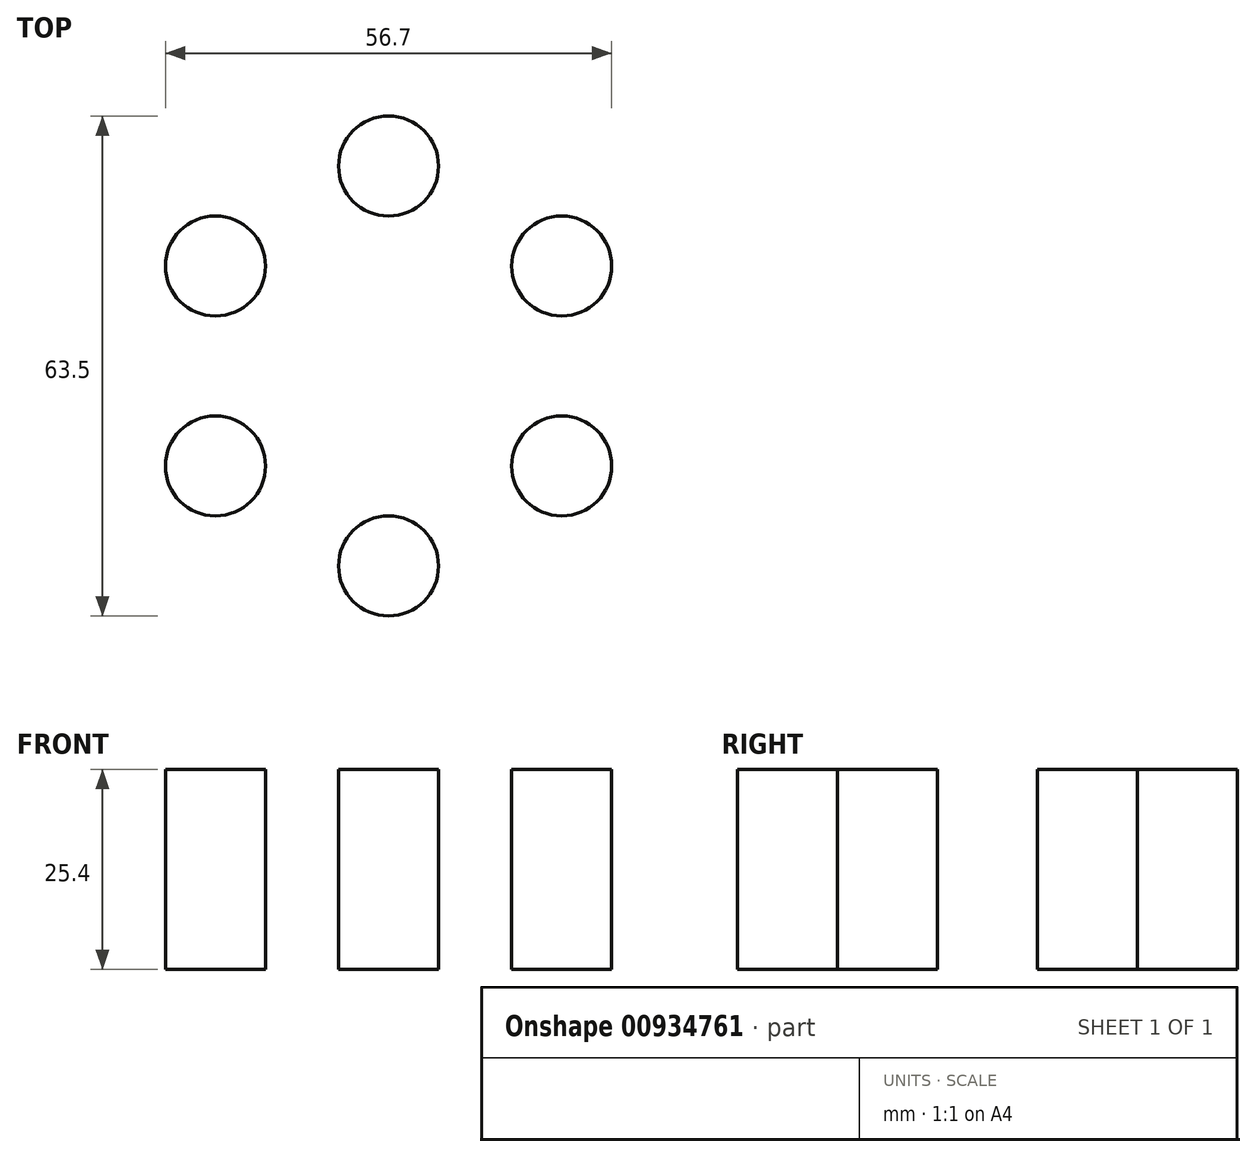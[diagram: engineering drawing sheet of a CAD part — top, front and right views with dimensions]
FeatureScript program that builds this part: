
annotation { "Feature Type Name" : "Feature", "Feature Type Description" : "" }
export const myFeature = defineFeature(function(context is Context, id is Id, definition is map)
    precondition{}
    {
        {
            var Q0;
            Q0=qCreatedBy(makeId("Top.planeOp"),FACE);
            var sketch = newSketch(context, id + "F0", { "sketchPlane" : qUnion([Q0])});
            skCircle(sketch, "E0.cCircle", {"center": v(0, 0) * mm, "radius": 22 * mm, "construction": true});
            skLineSegment(sketch, "E0.0", {"start": v(22, 12.7) * mm, "end": v(22, -12.7) * mm, "construction": true});
            skLineSegment(sketch, "E0.1", {"start": v(22, -12.7) * mm, "end": v(0, -25.4) * mm, "construction": true});
            skLineSegment(sketch, "E0.2", {"start": v(0, -25.4) * mm, "end": v(-22, -12.7) * mm, "construction": true});
            skLineSegment(sketch, "E0.3", {"start": v(-22, -12.7) * mm, "end": v(-22, 12.7) * mm, "construction": true});
            skLineSegment(sketch, "E0.4", {"start": v(-22, 12.7) * mm, "end": v(0, 25.4) * mm, "construction": true});
            skLineSegment(sketch, "E0.5", {"start": v(0, 25.4) * mm, "end": v(22, 12.7) * mm, "construction": true});
            skPoint(sketch, "E0.0.midPoint", {"position": v(22, 0) * mm});
            skCircle(sketch, "E1", {"center": v(0, 25.4) * mm, "radius": 6.35 * mm});
            skCircle(sketch, "E2.1.0", {"center": v(-22, -12.7) * mm, "radius": 6.35 * mm});
            skCircle(sketch, "E2.2.0", {"center": v(22, -12.7) * mm, "radius": 6.35 * mm});
            skCircle(sketch, "E3.1.0", {"center": v(22, 12.7) * mm, "radius": 6.35 * mm});
            skCircle(sketch, "E4.1.3.0", {"center": v(-22, 12.7) * mm, "radius": 6.35 * mm});
            skCircle(sketch, "E4.1.5.0", {"center": v(0, -25.4) * mm, "radius": 6.35 * mm});
            skSolve(sketch);
        }
        {
            var Q0;
            Q0 = qSketchRegion(id + "F0", true);
            extrude(context, id + "F1", {"entities" : qUnion([Q0]), "depth" : 25.4 * mm, "offsetDistance" : 25.4 * mm});
        }
    });
